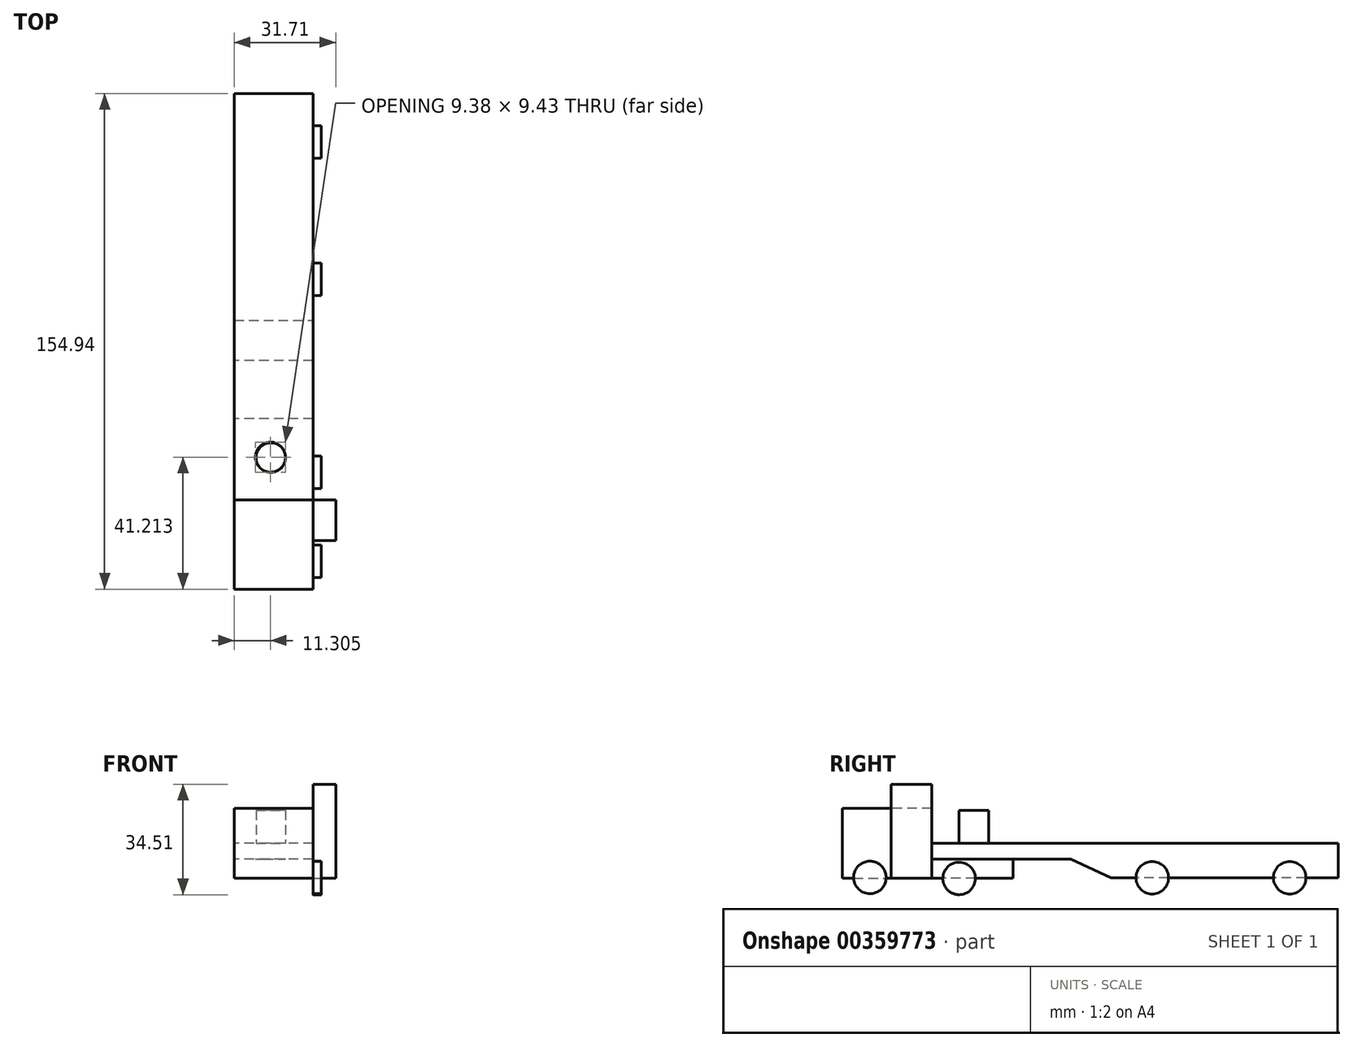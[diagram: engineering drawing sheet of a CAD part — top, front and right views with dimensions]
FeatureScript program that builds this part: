
annotation { "Feature Type Name" : "Feature", "Feature Type Description" : "" }
export const myFeature = defineFeature(function(context is Context, id is Id, definition is map)
    precondition{}
    {
        {
            var Q0;
            Q0=qCreatedBy(makeId("Front.planeOp"),FACE);
            var sketch = newSketch(context, id + "F0", { "sketchPlane" : qUnion([Q0])});
            skLineSegment(sketch, "E0.bottom", {"start": v(-13.77, -20.91) * mm, "end": v(10.8, -20.91) * mm});
            skLineSegment(sketch, "E0.top", {"start": v(-13.77, -42.71) * mm, "end": v(10.8, -42.71) * mm});
            skLineSegment(sketch, "E0.left", {"start": v(-13.77, -20.91) * mm, "end": v(-13.77, -42.71) * mm});
            skLineSegment(sketch, "E0.right", {"start": v(10.8, -20.91) * mm, "end": v(10.8, -42.71) * mm});
            skLineSegment(sketch, "E1.bottom", {"start": v(-18.53, -13.38) * mm, "end": v(17.94, -13.38) * mm});
            skLineSegment(sketch, "E1.top", {"start": v(-18.53, -48.66) * mm, "end": v(17.94, -48.66) * mm});
            skLineSegment(sketch, "E1.left", {"start": v(-18.53, -13.38) * mm, "end": v(-18.53, -48.66) * mm});
            skLineSegment(sketch, "E1.right", {"start": v(17.94, -13.38) * mm, "end": v(17.94, -48.66) * mm});
            skLineSegment(sketch, "E2", {"start": v(-13.77, -20.91) * mm, "end": v(0, -20.91) * mm});
            skSolve(sketch);
        }
        {
            var Q0;
            Q0=makeQuery(id+"F0.imprint","IMPRINT",FACE,{"disambiguationData":[TD([[makeQuery(id+"F0.imprint","IMPRINT",EDGE,{"derivedFrom":sQuery(id+"F0.wireOp",EDGE,"E0.bottom")}),-1.0]])]});
            extrude(context, id + "F1", {"entities" : qUnion([Q0]), "depth" : 27.94 * mm});
        }
        {
            var Q0;
            Q0=makeQuery(id+"F0.imprint","IMPRINT",FACE,{"disambiguationData":[TD([[makeQuery(id+"F0.imprint","IMPRINT",EDGE,{"derivedFrom":sQuery(id+"F0.wireOp",EDGE,"E0.bottom")}),1.0]])]});
            extrude(context, id + "F2", {"entities" : qUnion([Q0]), "operationType" : NewBodyOperationType.ADD, "depth" : 12.7 * mm});
        }
        {
            var Q0;
            Q0=makeQuery(id+"F2.opExtrude","CAP_FACE",FACE,{"disambiguationData":[OSD([sQuery(id+"F0.wireOp",EDGE,"E0.bottom"),sQuery(id+"F0.wireOp",EDGE,"E0.top"),sQuery(id+"F0.wireOp",EDGE,"E0.left"),sQuery(id+"F0.wireOp",EDGE,"E0.right"),sQuery(id+"F0.wireOp",EDGE,"E1.bottom"),sQuery(id+"F0.wireOp",EDGE,"E1.top"),sQuery(id+"F0.wireOp",EDGE,"E1.left"),sQuery(id+"F0.wireOp",EDGE,"E1.right")])],"isStart":false});
            var sketch = newSketch(context, id + "F3", { "sketchPlane" : qUnion([Q0])});
            skLineSegment(sketch, "E3", {"start": v(-13.77, -42.71) * mm, "end": v(-18.53, -42.71) * mm});
            skLineSegment(sketch, "E4", {"start": v(-18.53, -42.71) * mm, "end": v(17.94, -42.71) * mm});
            skSolve(sketch);
        }
        {
            var Q0;
            {var subQ0=makeQuery(id+"F2.opExtrude","CAP_EDGE",EDGE,{"disambiguationData":[OSD([sQuery(id+"F0.wireOp",EDGE,"E1.top")])],"isStart":false});Q0=makeQuery(id+"F3.imprint","IMPRINT",FACE,{"disambiguationData":[TD([[makeQuery(id+"F3.imprint","IMPRINT",EDGE,{"derivedFrom":subQ0}),1.0]])]});}
            extrude(context, id + "F4", {"entities" : qUnion([Q0]), "operationType" : NewBodyOperationType.REMOVE, "oppositeDirection" : true, "depth" : 25.4 * mm});
        }
        {
            var Q0;
            Q0=makeQuery(id+"F2.opExtrude","CAP_FACE",FACE,{"disambiguationData":[OSD([sQuery(id+"F0.wireOp",EDGE,"E0.bottom"),sQuery(id+"F0.wireOp",EDGE,"E0.top"),sQuery(id+"F0.wireOp",EDGE,"E0.left"),sQuery(id+"F0.wireOp",EDGE,"E0.right"),sQuery(id+"F0.wireOp",EDGE,"E1.bottom"),sQuery(id+"F0.wireOp",EDGE,"E1.top"),sQuery(id+"F0.wireOp",EDGE,"E1.left"),sQuery(id+"F0.wireOp",EDGE,"E1.right")])],"isStart":false});
            var sketch = newSketch(context, id + "F5", { "sketchPlane" : qUnion([Q0])});
            skLineSegment(sketch, "E5", {"start": v(10.8, -20.91) * mm, "end": v(10.8, -13.38) * mm});
            skSolve(sketch);
        }
        {
            var Q0;
            {var subQ6=sQuery(id+"F5.wireOp",EDGE,"E5");Q0=makeQuery(id+"F5.imprint","IMPRINT",FACE,{"disambiguationData":[TD([[makeQuery(id+"F5.imprint","IMPRINT",EDGE,{"derivedFrom":subQ6}),-1.0]])]});}
            var Q1;
            {var subQ6=sQuery(id+"F5.wireOp",EDGE,"E5");Q1=makeQuery(id+"F5.imprint","IMPRINT",FACE,{"disambiguationData":[TD([[makeQuery(id+"F5.imprint","IMPRINT",EDGE,{"derivedFrom":subQ6}),1.0]])]});}
            extrude(context, id + "F6", {"entities" : qUnion([Q0, Q1]), "operationType" : NewBodyOperationType.REMOVE, "oppositeDirection" : true, "depth" : 25.4 * mm});
        }
        {
            var Q0;
            Q0=makeQuery(id+"F0.imprint","IMPRINT",FACE,{"disambiguationData":[TD([[makeQuery(id+"F0.imprint","IMPRINT",EDGE,{"derivedFrom":sQuery(id+"F0.wireOp",EDGE,"E0.bottom")}),-1.0]])]});
            var sketch = newSketch(context, id + "F7", { "sketchPlane" : qUnion([Q0])});
            skLineSegment(sketch, "E6.bottom", {"start": v(11.18, -36.75) * mm, "end": v(-14.18, -36.75) * mm});
            skLineSegment(sketch, "E6.top", {"start": v(11.18, -31.84) * mm, "end": v(-14.18, -31.84) * mm});
            skLineSegment(sketch, "E6.left", {"start": v(11.18, -36.75) * mm, "end": v(11.18, -31.84) * mm});
            skLineSegment(sketch, "E6.right", {"start": v(-14.18, -36.75) * mm, "end": v(-14.18, -31.84) * mm});
            skSolve(sketch);
        }
        {
            var Q0;
            {var subQ0=sQuery(id+"F7.wireOp",EDGE,"E6.bottom");var subQ1=makeQuery(id+"F0.imprint","IMPRINT",EDGE,{"derivedFrom":sQuery(id+"F0.wireOp",EDGE,"E0.right")});var subQ2=makeQuery(id+"F7.imprint","INTERSECT",VERTEX,{"derivedFrom":[subQ1,subQ0]});Q0=makeQuery(id+"F7.imprint","IMPRINT",FACE,{"disambiguationData":[TD([[makeQuery(id+"F7.imprint","IMPRINT",EDGE,{"disambiguationData":[TD([[subQ2,-1.0]])],"derivedFrom":subQ0}),-1.0]])]});}
            var sketch = newSketch(context, id + "F8", { "sketchPlane" : qUnion([Q0])});
            skLineSegment(sketch, "E7.bottom", {"start": v(10.84, -31.84) * mm, "end": v(-13.78, -31.84) * mm});
            skLineSegment(sketch, "E7.top", {"start": v(10.84, -36.73) * mm, "end": v(-13.78, -36.73) * mm});
            skLineSegment(sketch, "E7.left", {"start": v(10.84, -31.84) * mm, "end": v(10.84, -36.73) * mm});
            skLineSegment(sketch, "E7.right", {"start": v(-13.78, -31.84) * mm, "end": v(-13.78, -36.73) * mm});
            skSolve(sketch);
        }
        {
            var Q0;
            {var subQ5=makeQuery(id+"F0.imprint","IMPRINT",EDGE,{"derivedFrom":sQuery(id+"F0.wireOp",EDGE,"E0.top")});Q0=makeQuery(id+"F7.imprint","IMPRINT",FACE,{"disambiguationData":[TD([[makeQuery(id+"F7.imprint","IMPRINT",EDGE,{"derivedFrom":subQ5}),1.0]])]});}
            extrude(context, id + "F9", {"entities" : qUnion([Q0]), "operationType" : NewBodyOperationType.ADD, "depth" : -25.4 * mm});
        }
        {
            var Q0;
            Q0=makeQuery(id+"F9.opExtrude","SWEPT_FACE",FACE,{"disambiguationData":[OSD([sQuery(id+"F7.wireOp",EDGE,"E6.bottom")])]});
            var sketch = newSketch(context, id + "F10", { "sketchPlane" : qUnion([Q0])});
            skCircle(sketch, "E8", {"center": v(-2.36, 13.16) * mm, "radius": 4.61 * mm});
            skSolve(sketch);
        }
        {
            var Q0;
            {var subQ2=makeQuery(id+"F0.imprint","IMPRINT",EDGE,{"derivedFrom":sQuery(id+"F0.wireOp",EDGE,"E0.right")});var subQ3=sQuery(id+"F7.wireOp",EDGE,"E6.top");var subQ4=makeQuery(id+"F7.imprint","INTERSECT",VERTEX,{"derivedFrom":[subQ2,subQ3]});var subQ11=makeQuery(id+"F7.imprint","IMPRINT",EDGE,{"disambiguationData":[TD([[subQ4,-1.0]])],"derivedFrom":subQ3});Q0=makeQuery(id+"F8.imprint","IMPRINT",FACE,{"disambiguationData":[TD([[makeQuery(id+"F8.imprint","IMPRINT",EDGE,{"derivedFrom":subQ11}),1.0]])]});}
            extrude(context, id + "F11", {"entities" : qUnion([Q0]), "depth" : -127 * mm});
        }
        {
            var Q0;
            Q0=makeQuery(id+"F11.opExtrude","SWEPT_FACE",FACE,{"disambiguationData":[OSD([sQuery(id+"F7.wireOp",EDGE,"E6.top")])]});
            var sketch = newSketch(context, id + "F12", { "sketchPlane" : qUnion([Q0])});
            skCircle(sketch, "E9", {"center": v(-2.47, 13.32) * mm, "radius": 4.7 * mm});
            skSolve(sketch);
        }
        {
            var Q0;
            Q0=makeQuery(id+"F12.imprint","IMPRINT",FACE,{"disambiguationData":[TD([[makeQuery(id+"F12.imprint","IMPRINT",EDGE,{"derivedFrom":sQuery(id+"F12.wireOp",EDGE,"E9")}),1.0]])]});
            extrude(context, id + "F13", {"entities" : qUnion([Q0]), "operationType" : NewBodyOperationType.ADD, "oppositeDirection" : true, "depth" : 10.16 * mm});
        }
        {
            var Q0;
            Q0=makeQuery(id+"F10.imprint","IMPRINT",FACE,{"disambiguationData":[TD([[makeQuery(id+"F10.imprint","IMPRINT",EDGE,{"derivedFrom":sQuery(id+"F10.wireOp",EDGE,"E8")}),1.0]])]});
            extrude(context, id + "F14", {"entities" : qUnion([Q0]), "operationType" : NewBodyOperationType.ADD, "depth" : 15.24 * mm});
        }
        {
            var Q0;
            Q0=makeQuery(id+"F11.opExtrude","SWEPT_FACE",FACE,{"disambiguationData":[OSD([sQuery(id+"F0.wireOp",EDGE,"E0.right")])]});
            var sketch = newSketch(context, id + "F15", { "sketchPlane" : qUnion([Q0])});
            skCircle(sketch, "E10", {"center": v(-19.29, -42.5) * mm, "radius": 5.08 * mm});
            skCircle(sketch, "E11", {"center": v(8.59, -42.81) * mm, "radius": 5.08 * mm});
            skSolve(sketch);
        }
        {
            var Q0;
            Q0=makeQuery(id+"F11.opExtrude","SWEPT_FACE",FACE,{"disambiguationData":[OSD([sQuery(id+"F8.wireOp",EDGE,"E7.top")])]});
            var sketch = newSketch(context, id + "F16", { "sketchPlane" : qUnion([Q0])});
            skLineSegment(sketch, "E12.bottom", {"start": v(10.8, -43.45) * mm, "end": v(-13.77, -43.45) * mm});
            skLineSegment(sketch, "E12.top", {"start": v(10.8, -127) * mm, "end": v(-13.77, -127) * mm});
            skLineSegment(sketch, "E12.left", {"start": v(10.8, -43.45) * mm, "end": v(10.8, -127) * mm});
            skLineSegment(sketch, "E12.right", {"start": v(-13.77, -43.45) * mm, "end": v(-13.77, -127) * mm});
            skSolve(sketch);
        }
        {
            var Q0;
            Q0 = qSketchRegion(id + "F16", true);
            extrude(context, id + "F17", {"entities" : qUnion([Q0]), "operationType" : NewBodyOperationType.ADD, "depth" : 5.84 * mm});
        }
        {
            var Q0;
            Q0=makeQuery(id+"F17.boolean.opBoolean","MERGE",FACE,{"derivedFrom":[makeQuery(id+"F11.opExtrude","SWEPT_FACE",FACE,{"disambiguationData":[OSD([sQuery(id+"F0.wireOp",EDGE,"E0.right")])]}),makeQuery(id+"F17.opExtrude","SWEPT_FACE",FACE,{"disambiguationData":[OSD([sQuery(id+"F16.wireOp",EDGE,"E12.left")])]})]});
            var sketch = newSketch(context, id + "F18", { "sketchPlane" : qUnion([Q0])});
            skLineSegment(sketch, "E13", {"start": v(56.02, -42.57) * mm, "end": v(43.45, -36.73) * mm});
            skSolve(sketch);
        }
        {
            var Q0;
            {var subQ0=sQuery(id+"F18.wireOp",EDGE,"E13");Q0=makeQuery(id+"F18.imprint","IMPRINT",FACE,{"disambiguationData":[TD([[makeQuery(id+"F18.imprint","IMPRINT",EDGE,{"derivedFrom":subQ0}),1.0]])]});}
            extrude(context, id + "F19", {"entities" : qUnion([Q0]), "operationType" : NewBodyOperationType.REMOVE, "oppositeDirection" : true, "depth" : 25.4 * mm});
        }
        {
            var Q0;
            Q0=makeQuery(id+"F17.boolean.opBoolean","MERGE",FACE,{"derivedFrom":[makeQuery(id+"F11.opExtrude","SWEPT_FACE",FACE,{"disambiguationData":[OSD([sQuery(id+"F0.wireOp",EDGE,"E0.right")])]}),makeQuery(id+"F17.opExtrude","SWEPT_FACE",FACE,{"disambiguationData":[OSD([sQuery(id+"F16.wireOp",EDGE,"E12.left")])]})]});
            var sketch = newSketch(context, id + "F20", { "sketchPlane" : qUnion([Q0])});
            skCircle(sketch, "E14", {"center": v(68.93, -42.57) * mm, "radius": 5.08 * mm});
            skCircle(sketch, "E15", {"center": v(111.9, -42.57) * mm, "radius": 5.08 * mm});
            skSolve(sketch);
        }
        {
            var Q0;
            {var subQ0=sQuery(id+"F20.wireOp",EDGE,"E14");var subQ1=makeQuery(id+"F17.opExtrude","CAP_EDGE",EDGE,{"disambiguationData":[OSD([sQuery(id+"F16.wireOp",EDGE,"E12.left")])],"isStart":false});var subQ2=makeQuery(id+"F20.imprint","INTERSECT",VERTEX,{"disambiguationData":[OD(0.0)],"derivedFrom":[subQ1,subQ0]});Q0=makeQuery(id+"F20.imprint","IMPRINT",FACE,{"disambiguationData":[TD([[makeQuery(id+"F20.imprint","IMPRINT",EDGE,{"disambiguationData":[TD([[subQ2,-1.0]])],"derivedFrom":subQ0}),1.0]])]});}
            var Q1;
            {var subQ0=sQuery(id+"F20.wireOp",EDGE,"E15");var subQ1=makeQuery(id+"F17.opExtrude","CAP_EDGE",EDGE,{"disambiguationData":[OSD([sQuery(id+"F16.wireOp",EDGE,"E12.left")])],"isStart":false});var subQ2=makeQuery(id+"F20.imprint","INTERSECT",VERTEX,{"disambiguationData":[OD(0.0)],"derivedFrom":[subQ1,subQ0]});Q1=makeQuery(id+"F20.imprint","IMPRINT",FACE,{"disambiguationData":[TD([[makeQuery(id+"F20.imprint","IMPRINT",EDGE,{"disambiguationData":[TD([[subQ2,1.0]])],"derivedFrom":subQ0}),1.0]])]});}
            var Q2;
            Q2=makeQuery(id+"F15.imprint","IMPRINT",FACE,{"disambiguationData":[TD([[makeQuery(id+"F15.imprint","IMPRINT",EDGE,{"derivedFrom":sQuery(id+"F15.wireOp",EDGE,"E10")}),1.0]])]});
            var Q3;
            Q3=makeQuery(id+"F15.imprint","IMPRINT",FACE,{"disambiguationData":[TD([[makeQuery(id+"F15.imprint","IMPRINT",EDGE,{"derivedFrom":sQuery(id+"F15.wireOp",EDGE,"E11")}),1.0]])]});
            var Q4;
            {var subQ0=sQuery(id+"F20.wireOp",EDGE,"E14");var subQ1=makeQuery(id+"F17.opExtrude","CAP_EDGE",EDGE,{"disambiguationData":[OSD([sQuery(id+"F16.wireOp",EDGE,"E12.left")])],"isStart":false});var subQ2=makeQuery(id+"F20.imprint","INTERSECT",VERTEX,{"disambiguationData":[OD(0.0)],"derivedFrom":[subQ1,subQ0]});Q4=makeQuery(id+"F20.imprint","IMPRINT",FACE,{"disambiguationData":[TD([[makeQuery(id+"F20.imprint","IMPRINT",EDGE,{"disambiguationData":[TD([[subQ2,1.0]])],"derivedFrom":subQ0}),1.0]])]});}
            var Q5;
            {var subQ0=sQuery(id+"F20.wireOp",EDGE,"E15");var subQ1=makeQuery(id+"F17.opExtrude","CAP_EDGE",EDGE,{"disambiguationData":[OSD([sQuery(id+"F16.wireOp",EDGE,"E12.left")])],"isStart":false});var subQ2=makeQuery(id+"F20.imprint","INTERSECT",VERTEX,{"disambiguationData":[OD(0.0)],"derivedFrom":[subQ1,subQ0]});Q5=makeQuery(id+"F20.imprint","IMPRINT",FACE,{"disambiguationData":[TD([[makeQuery(id+"F20.imprint","IMPRINT",EDGE,{"disambiguationData":[TD([[subQ2,-1.0]])],"derivedFrom":subQ0}),1.0]])]});}
            extrude(context, id + "F21", {"entities" : qUnion([Q0, Q1, Q2, Q3, Q4, Q5]), "operationType" : NewBodyOperationType.ADD, "depth" : 2.54 * mm});
        }
    });
